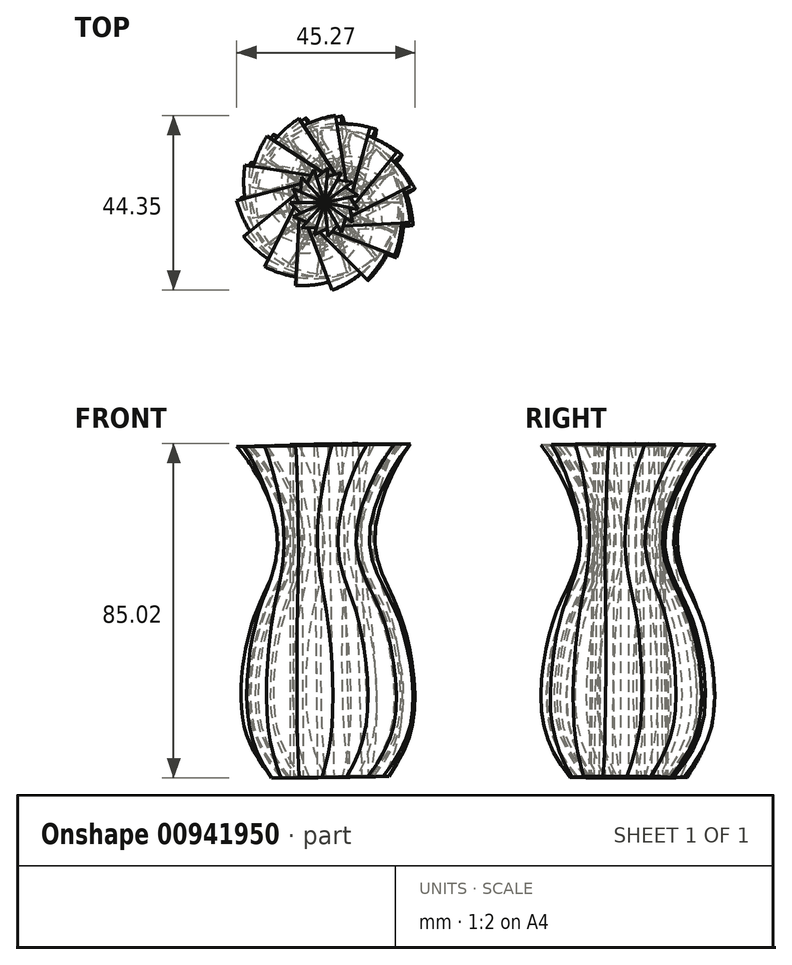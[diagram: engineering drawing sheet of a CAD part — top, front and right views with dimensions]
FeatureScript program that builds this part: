
annotation { "Feature Type Name" : "Feature", "Feature Type Description" : "" }
export const myFeature = defineFeature(function(context is Context, id is Id, definition is map)
    precondition{}
    {
        {
            var Q0;
            Q0=qCreatedBy(makeId("Front.planeOp"),FACE);
            var sketch = newSketch(context, id + "F0", { "sketchPlane" : qUnion([Q0])});
            skLineSegment(sketch, "E0", {"start": v(0, 39.27) * mm, "end": v(0, -45.16) * mm});
            skLineSegment(sketch, "E1", {"start": v(0, -45.16) * mm, "end": v(20.34, -45.16) * mm});
            skLineSegment(sketch, "E2", {"start": v(0, 39.27) * mm, "end": v(27.62, 39.27) * mm});
            skPoint(sketch, "E3.endSnap0", {"position": v(10.17, -45.16) * mm});
            skFitSpline(sketch, "E4", {"points": [v(27.62, 39.27) * mm, v(17.15, 15.94) * mm, v(22.23, 0) * mm, v(26.53, -12.2) * mm, v(27.62, -30.65) * mm, v(20.34, -45.16) * mm], "startDerivative": vector(-55.1, -63.1) * mm, "endDerivative": vector(-59.66, -74.58) * mm});
            skLineSegment(sketch, "E5", {"start": v(9.38, -0.88) * mm, "end": v(9.7, -21.6) * mm});
            skSolve(sketch);
        }
        {
            var Q0;
            {var subQ0=sQuery(id+"F0.wireOp",EDGE,"E0");Q0=makeQuery(id+"F0.imprint","IMPRINT",FACE,{"disambiguationData":[TD([[makeQuery(id+"F0.imprint","IMPRINT",EDGE,{"derivedFrom":subQ0}),1.0]])]});}
            var Q1;
            Q1=sQuery(id+"F0.wireOp",EDGE,"E0");
            revolve(context, id + "F1", {"surfaceOperationType" : NewSurfaceOperationType.NEW, "entities" : qUnion([Q0]), "axis" : qUnion([Q1]), "revolveType" : RevolveType.ONE_DIRECTION, "angle" : 45 * degree});
        }
        {
            var Q0;
            Q0=makeQuery(id+"F1.opRevolve","SWEPT_BODY",BODY,{"disambiguationData":[OSD([sQuery(id+"F0.wireOp",EDGE,"E0"),sQuery(id+"F0.wireOp",EDGE,"E1"),sQuery(id+"F0.wireOp",EDGE,"E2"),sQuery(id+"F0.wireOp",EDGE,"e89406fa-a3c8-4e77-b4de-1d4cb888b24e")])]});
            var Q1;
            Q1=sQuery(id+"F0.wireOp",EDGE,"E5");
            circularPattern(context, id + "F2", {"entities" : qUnion([Q0]), "axis" : qUnion([Q1]), "angle" : 360 * degree, "instanceCount" : 15, "equalSpace" : true});
        }
    });
